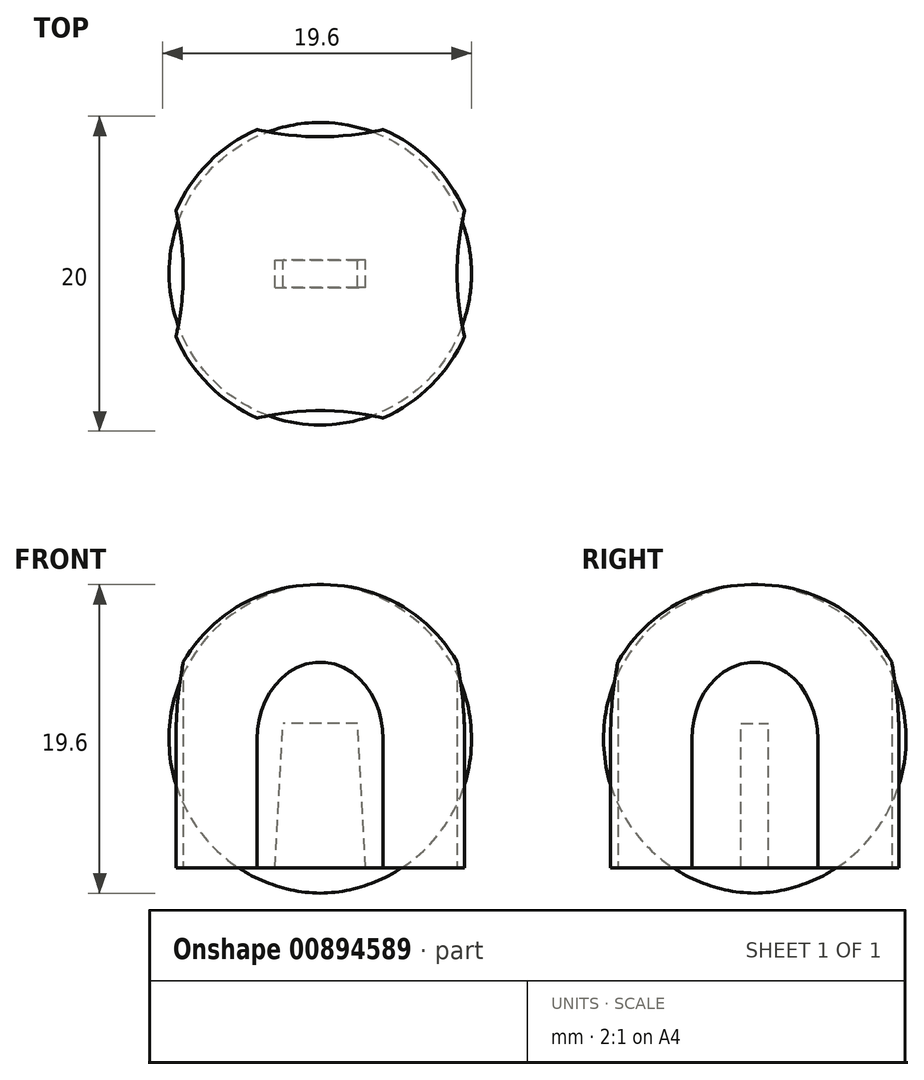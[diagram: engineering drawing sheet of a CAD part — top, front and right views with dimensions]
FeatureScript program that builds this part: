
annotation { "Feature Type Name" : "Feature", "Feature Type Description" : "" }
export const myFeature = defineFeature(function(context is Context, id is Id, definition is map)
    precondition{}
    {
        {
            var Q0;
            Q0=qCreatedBy(makeId("Front.planeOp"),FACE);
            var sketch = newSketch(context, id + "F0", { "sketchPlane" : qUnion([Q0])});
            skLineSegment(sketch, "E0", {"start": v(0, 0) * mm, "end": v(10, 0) * mm});
            skLineSegment(sketch, "E1", {"start": v(0, 0) * mm, "end": v(0, 18) * mm});
            skLineSegment(sketch, "E2", {"start": v(10, 0) * mm, "end": v(10, 8.2) * mm});
            skArc(sketch, "E3", {"start": v(10, 8.2) * mm, "mid": v(7.06, 15.2) * mm, "end": v(0, 18) * mm});
            skSolve(sketch);
        }
        {
            var Q0;
            Q0=makeQuery(id+"F0.imprint","IMPRINT",FACE,{"disambiguationData":[TD([[makeQuery(id+"F0.imprint","IMPRINT",EDGE,{"derivedFrom":sQuery(id+"F0.wireOp",EDGE,"E0")}),1.0]])]});
            var Q1;
            Q1=sQuery(id+"F0.wireOp",EDGE,"E1");
            revolve(context, id + "F1", {"surfaceOperationType" : NewSurfaceOperationType.NEW, "entities" : qUnion([Q0]), "axis" : qUnion([Q1]), "revolveType" : RevolveType.FULL});
        }
        {
            var Q0;
            Q0=makeQuery(id+"F1.opRevolve","SWEPT_FACE",FACE,{"disambiguationData":[OSD([sQuery(id+"F0.wireOp",EDGE,"E0")])]});
            var sketch = newSketch(context, id + "F2", { "sketchPlane" : qUnion([Q0])});
            skArc(sketch, "E4", {"start": v(-4, 9.17) * mm, "mid": v(0, 8.7) * mm, "end": v(4, 9.17) * mm});
            skArc(sketch, "E5.1.0", {"start": v(-9.17, -4) * mm, "mid": v(-8.7, 0) * mm, "end": v(-9.17, 4) * mm});
            skArc(sketch, "E5.2.0", {"start": v(4, -9.17) * mm, "mid": v(0, -8.7) * mm, "end": v(-4, -9.17) * mm});
            skArc(sketch, "E5.3.0", {"start": v(9.17, 4) * mm, "mid": v(8.7, 0) * mm, "end": v(9.17, -4) * mm});
            skPoint(sketch, "E5.center", {"position": v(0, 0) * mm});
            skPoint(sketch, "E6", {"position": v(0, 8.7) * mm});
            skSolve(sketch);
        }
        {
            var Q0;
            {var subQ0=sQuery(id+"F2.wireOp",EDGE,"E4");Q0=makeQuery(id+"F2.imprint","IMPRINT",FACE,{"disambiguationData":[TD([[makeQuery(id+"F2.imprint","IMPRINT",EDGE,{"derivedFrom":subQ0}),1.0]])]});}
            var Q1;
            {var subQ0=sQuery(id+"F2.wireOp",EDGE,"E5.1.0");Q1=makeQuery(id+"F2.imprint","IMPRINT",FACE,{"disambiguationData":[TD([[makeQuery(id+"F2.imprint","IMPRINT",EDGE,{"derivedFrom":subQ0}),1.0]])]});}
            var Q2;
            {var subQ0=sQuery(id+"F2.wireOp",EDGE,"E5.2.0");Q2=makeQuery(id+"F2.imprint","IMPRINT",FACE,{"disambiguationData":[TD([[makeQuery(id+"F2.imprint","IMPRINT",EDGE,{"derivedFrom":subQ0}),1.0]])]});}
            var Q3;
            {var subQ0=sQuery(id+"F2.wireOp",EDGE,"E5.3.0");Q3=makeQuery(id+"F2.imprint","IMPRINT",FACE,{"disambiguationData":[TD([[makeQuery(id+"F2.imprint","IMPRINT",EDGE,{"derivedFrom":subQ0}),1.0]])]});}
            extrude(context, id + "F3", {"entities" : qUnion([Q0, Q1, Q2, Q3]), "operationType" : NewBodyOperationType.REMOVE, "oppositeDirection" : true, "depth" : 25 * mm, "offsetDistance" : 25 * mm});
        }
        {
            var Q0;
            Q0=qCreatedBy(makeId("Front.planeOp"),FACE);
            var sketch = newSketch(context, id + "F4", { "sketchPlane" : qUnion([Q0])});
            skLineSegment(sketch, "E7", {"start": v(-2.87, 0) * mm, "end": v(-2.37, 9.2) * mm});
            skLineSegment(sketch, "E8", {"start": v(-2.38, 9.2) * mm, "end": v(0, 9.2) * mm});
            skLineSegment(sketch, "E9.MirrorCS", {"start": v(2.38, 9.2) * mm, "end": v(0, 9.2) * mm});
            skLineSegment(sketch, "E10.MirrorCS", {"start": v(2.88, 0) * mm, "end": v(2.38, 9.2) * mm});
            skLineSegment(sketch, "E11", {"start": v(-2.87, 0) * mm, "end": v(2.88, 0) * mm});
            skSolve(sketch);
        }
        {
            var Q0;
            Q0 = qSketchRegion(id + "F4", true);
            var Q1;
            Q1=sQuery(id+"F4.wireOp",EDGE,"E7");
            var Q2;
            Q2=sQuery(id+"F4.wireOp",EDGE,"E8");
            var Q3;
            Q3=sQuery(id+"F4.wireOp",EDGE,"E9.MirrorCS");
            var Q4;
            Q4=sQuery(id+"F4.wireOp",EDGE,"E10.MirrorCS");
            var Q5;
            Q5=sQuery(id+"F4.wireOp",EDGE,"E11");
            extrude(context, id + "F5", {"entities" : qUnion([Q0]), "operationType" : NewBodyOperationType.REMOVE, "surfaceEntities" : qUnion([Q1, Q2, Q3, Q4, Q5]), "endBound" : BoundingType.SYMMETRIC, "depth" : ((2.5 / 2) + .5) * mm, "offsetDistance" : 25 * mm});
        }
    });
